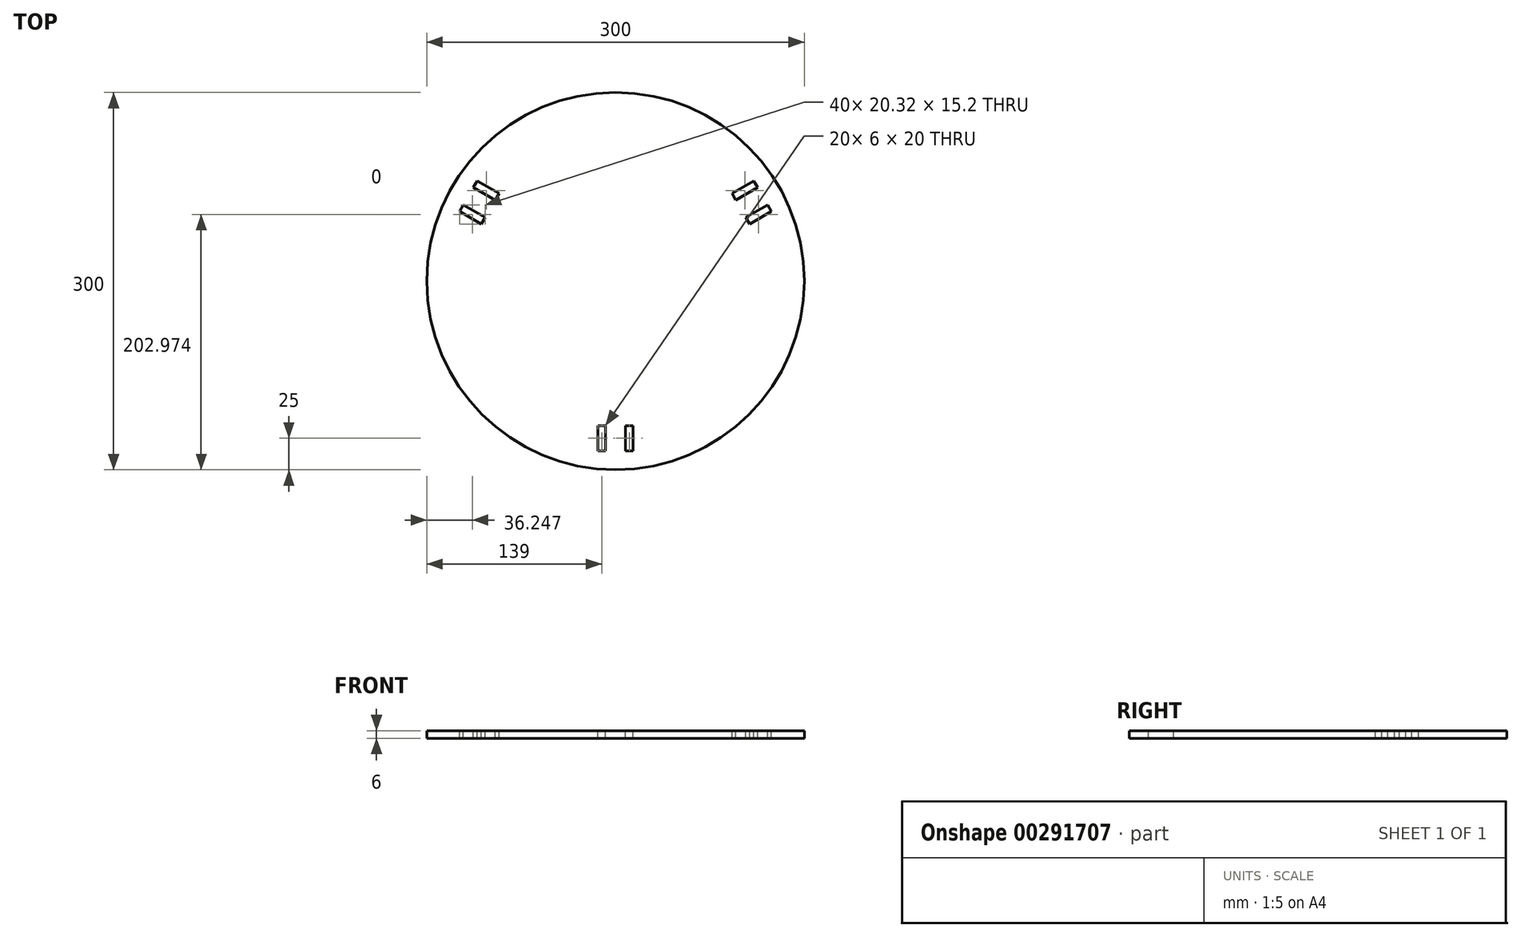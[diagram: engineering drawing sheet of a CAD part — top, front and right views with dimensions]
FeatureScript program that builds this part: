
annotation { "Feature Type Name" : "Feature", "Feature Type Description" : "" }
export const myFeature = defineFeature(function(context is Context, id is Id, definition is map)
    precondition{}
    {
        {
            var Q0;
            Q0=qCreatedBy(makeId("Top.planeOp"),FACE);
            var sketch = newSketch(context, id + "F0", { "sketchPlane" : qUnion([Q0])});
            skCircle(sketch, "E0", {"center": v(0, 0) * mm, "radius": 150 * mm});
            skSolve(sketch);
        }
        {
            var Q0;
            Q0=qSketchRegion(id+"F0",true);
            extrude(context, id + "F1", {"entities" : qUnion([Q0]), "depth" : 6 * mm});
        }
        {
            var Q0;
            Q0=makeQuery(id+"F1.opExtrude","CAP_FACE",FACE,{"disambiguationData":[OSD([sQuery(id+"F0.wireOp",EDGE,"E0")])],"isStart":false});
            var sketch = newSketch(context, id + "F2", { "sketchPlane" : qUnion([Q0])});
            skLineSegment(sketch, "E1", {"start": v(0, 0) * mm, "end": v(0, -125) * mm, "construction": true});
            skLineSegment(sketch, "E2.bottom", {"start": v(-14, -115) * mm, "end": v(-8, -115) * mm});
            skLineSegment(sketch, "E2.top", {"start": v(-14, -135) * mm, "end": v(-8, -135) * mm});
            skLineSegment(sketch, "E2.left", {"start": v(-14, -115) * mm, "end": v(-14, -135) * mm});
            skLineSegment(sketch, "E2.right", {"start": v(-8, -115) * mm, "end": v(-8, -135) * mm});
            skLineSegment(sketch, "E3.MirrorCS", {"start": v(8, -115) * mm, "end": v(8, -135) * mm});
            skLineSegment(sketch, "E4.MirrorCS", {"start": v(14, -115) * mm, "end": v(14, -135) * mm});
            skLineSegment(sketch, "E5.MirrorCS", {"start": v(14, -115) * mm, "end": v(8, -115) * mm});
            skLineSegment(sketch, "E6.MirrorCS", {"start": v(14, -135) * mm, "end": v(8, -135) * mm});
            skLineSegment(sketch, "E7", {"start": v(-8, -125) * mm, "end": v(8, -125) * mm, "construction": true});
            skLineSegment(sketch, "E8.1.0", {"start": v(106.6, 45.38) * mm, "end": v(103.6, 50.57) * mm});
            skLineSegment(sketch, "E8.1.1", {"start": v(123.91, 55.38) * mm, "end": v(120.91, 60.57) * mm});
            skLineSegment(sketch, "E8.1.2", {"start": v(106.6, 45.38) * mm, "end": v(123.91, 55.38) * mm});
            skLineSegment(sketch, "E8.1.3", {"start": v(103.6, 50.57) * mm, "end": v(120.91, 60.57) * mm});
            skLineSegment(sketch, "E8.1.4", {"start": v(95.6, 64.43) * mm, "end": v(112.91, 74.43) * mm});
            skLineSegment(sketch, "E8.1.5", {"start": v(112.25, 55.57) * mm, "end": v(104.25, 69.43) * mm, "construction": true});
            skLineSegment(sketch, "E8.1.6", {"start": v(109.91, 79.62) * mm, "end": v(112.91, 74.43) * mm});
            skLineSegment(sketch, "E8.1.7", {"start": v(92.6, 69.62) * mm, "end": v(95.6, 64.43) * mm});
            skLineSegment(sketch, "E8.1.8", {"start": v(92.6, 69.62) * mm, "end": v(109.91, 79.62) * mm});
            skLineSegment(sketch, "E8.1.9", {"start": v(0, 0) * mm, "end": v(108.25, 62.5) * mm, "construction": true});
            skLineSegment(sketch, "E8.2.0", {"start": v(-92.6, 69.62) * mm, "end": v(-95.6, 64.43) * mm});
            skLineSegment(sketch, "E8.2.1", {"start": v(-109.91, 79.62) * mm, "end": v(-112.91, 74.43) * mm});
            skLineSegment(sketch, "E8.2.2", {"start": v(-92.6, 69.62) * mm, "end": v(-109.91, 79.62) * mm});
            skLineSegment(sketch, "E8.2.3", {"start": v(-95.6, 64.43) * mm, "end": v(-112.91, 74.43) * mm});
            skLineSegment(sketch, "E8.2.4", {"start": v(-103.6, 50.57) * mm, "end": v(-120.91, 60.57) * mm});
            skLineSegment(sketch, "E8.2.5", {"start": v(-104.25, 69.43) * mm, "end": v(-112.25, 55.57) * mm, "construction": true});
            skLineSegment(sketch, "E8.2.6", {"start": v(-123.91, 55.38) * mm, "end": v(-120.91, 60.57) * mm});
            skLineSegment(sketch, "E8.2.7", {"start": v(-106.6, 45.38) * mm, "end": v(-103.6, 50.57) * mm});
            skLineSegment(sketch, "E8.2.8", {"start": v(-106.6, 45.38) * mm, "end": v(-123.91, 55.38) * mm});
            skLineSegment(sketch, "E8.2.9", {"start": v(0, 0) * mm, "end": v(-108.25, 62.5) * mm, "construction": true});
            skPoint(sketch, "E8.center", {"position": v(0, 0) * mm});
            skSolve(sketch);
        }
        {
            var Q0;
            Q0=qSketchRegion(id+"F2",true);
            extrude(context, id + "F3", {"entities" : qUnion([Q0]), "operationType" : NewBodyOperationType.REMOVE, "endBound" : BoundingType.THROUGH_ALL, "oppositeDirection" : true, "depth" : 25 * mm});
        }
    });
